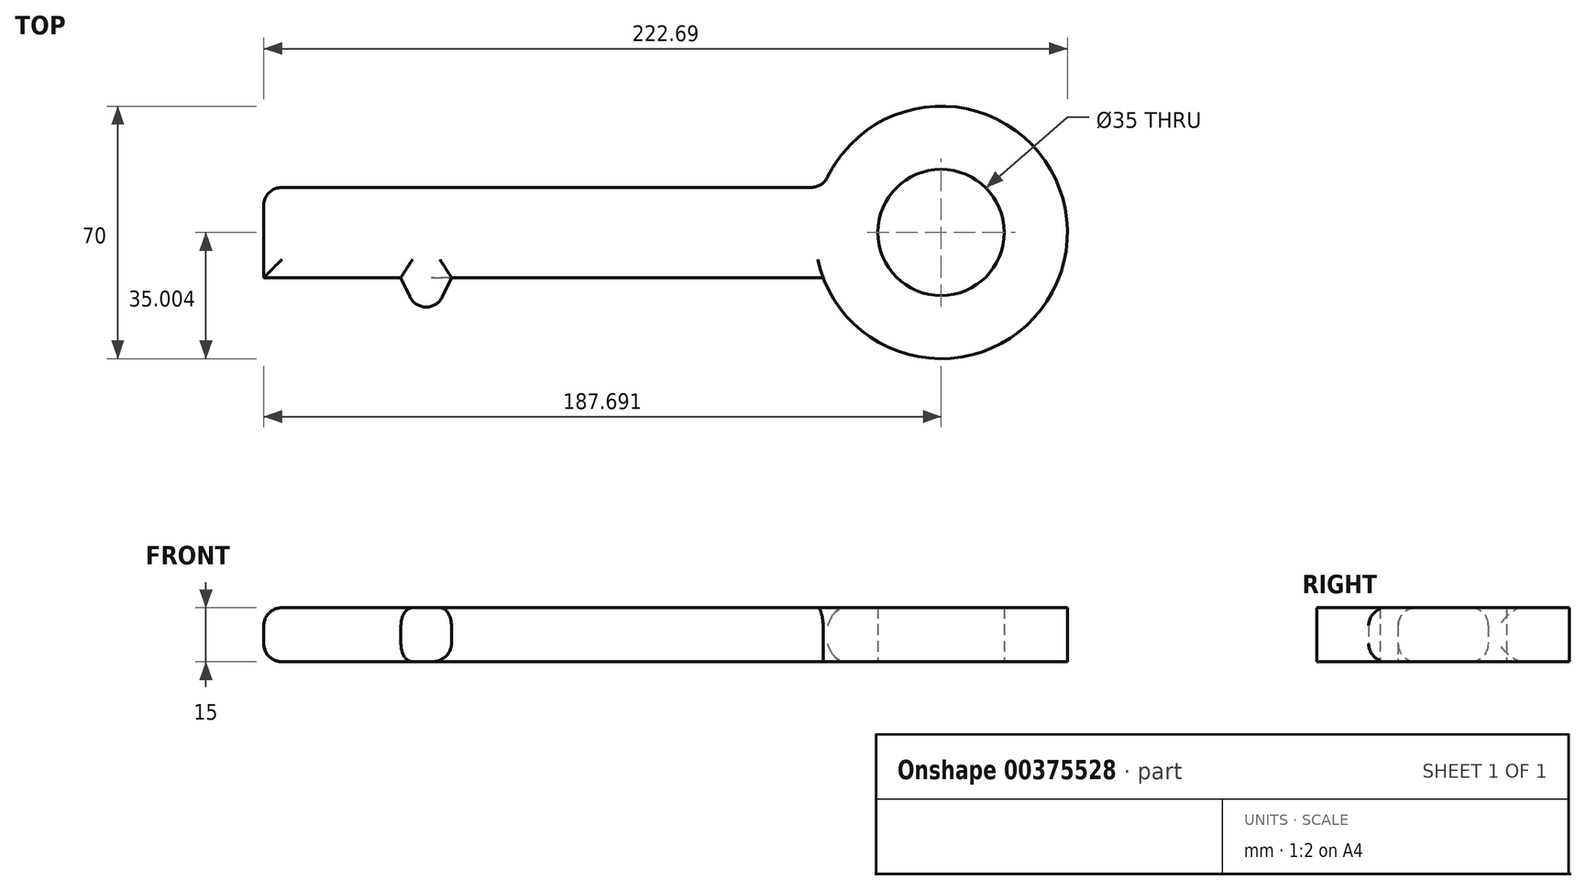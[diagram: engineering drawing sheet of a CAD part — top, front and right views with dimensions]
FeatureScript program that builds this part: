
annotation { "Feature Type Name" : "Feature", "Feature Type Description" : "" }
export const myFeature = defineFeature(function(context is Context, id is Id, definition is map)
    precondition{}
    {
        {
            var Q0;
            Q0=qCreatedBy(makeId("Top.planeOp"),FACE);
            var sketch = newSketch(context, id + "F0", { "sketchPlane" : qUnion([Q0])});
            skLineSegment(sketch, "E0.bottom", {"start": v(-78.27, 57.92) * mm, "end": v(76.73, 57.92) * mm});
            skLineSegment(sketch, "E0.top", {"start": v(-78.27, 32.92) * mm, "end": v(76.73, 32.92) * mm});
            skLineSegment(sketch, "E0.left", {"start": v(-78.27, 57.92) * mm, "end": v(-78.27, 32.92) * mm});
            skLineSegment(sketch, "E0.right", {"start": v(76.73, 57.92) * mm, "end": v(76.73, 32.92) * mm});
            skLineSegment(sketch, "E1.bottom", {"start": v(-78.27, 32.92) * mm, "end": v(-68.27, 32.92) * mm});
            skLineSegment(sketch, "E1.top", {"start": v(-78.27, 2.92) * mm, "end": v(-68.27, 2.92) * mm});
            skLineSegment(sketch, "E1.left", {"start": v(-78.27, 32.92) * mm, "end": v(-78.27, 2.92) * mm});
            skLineSegment(sketch, "E1.right", {"start": v(-68.27, 32.92) * mm, "end": v(-68.27, 2.92) * mm});
            skLineSegment(sketch, "E2.bottom", {"start": v(-58.27, 32.92) * mm, "end": v(-50.27, 32.92) * mm});
            skLineSegment(sketch, "E2.top", {"start": v(-58.27, 17.92) * mm, "end": v(-50.27, 17.92) * mm});
            skLineSegment(sketch, "E2.left", {"start": v(-58.27, 32.92) * mm, "end": v(-58.27, 17.92) * mm});
            skLineSegment(sketch, "E2.right", {"start": v(-50.27, 32.92) * mm, "end": v(-50.27, 17.92) * mm});
            skLineSegment(sketch, "E3", {"start": v(-33.27, 17.92) * mm, "end": v(-40.27, 32.92) * mm});
            skLineSegment(sketch, "E4", {"start": v(-40.27, 32.92) * mm, "end": v(-26.27, 32.92) * mm});
            skLineSegment(sketch, "E5", {"start": v(-26.27, 32.92) * mm, "end": v(-33.27, 17.92) * mm});
            skArc(sketch, "E6", {"start": v(76.73, 32.92) * mm, "mid": v(144.42, 45.42) * mm, "end": v(76.73, 57.92) * mm});
            skCircle(sketch, "E7", {"center": v(109.42, 45.42) * mm, "radius": 17.5 * mm});
            skSolve(sketch);
        }
        {
            var Q0;
            Q0=makeQuery(id+"F0.imprint","IMPRINT",FACE,{"disambiguationData":[TD([[makeQuery(id+"F0.imprint","IMPRINT",EDGE,{"derivedFrom":sQuery(id+"F0.wireOp",EDGE,"E0.bottom")}),-1.0]])]});
            var Q1;
            Q1=makeQuery(id+"F0.imprint","IMPRINT",FACE,{"disambiguationData":[TD([[makeQuery(id+"F0.imprint","IMPRINT",EDGE,{"derivedFrom":sQuery(id+"F0.wireOp",EDGE,"E3")}),-1.0]])]});
            var Q2;
            Q2=makeQuery(id+"F0.imprint","IMPRINT",FACE,{"disambiguationData":[TD([[makeQuery(id+"F0.imprint","IMPRINT",EDGE,{"derivedFrom":sQuery(id+"F0.wireOp",EDGE,"E2.bottom")}),-1.0]])]});
            var Q3;
            Q3=makeQuery(id+"F0.imprint","IMPRINT",FACE,{"disambiguationData":[TD([[makeQuery(id+"F0.imprint","IMPRINT",EDGE,{"derivedFrom":sQuery(id+"F0.wireOp",EDGE,"E1.bottom")}),-1.0]])]});
            var Q4;
            Q4=makeQuery(id+"F0.imprint","IMPRINT",FACE,{"disambiguationData":[TD([[makeQuery(id+"F0.imprint","IMPRINT",EDGE,{"derivedFrom":sQuery(id+"F0.wireOp",EDGE,"E0.right")}),1.0]])]});
            extrude(context, id + "F1", {"entities" : qUnion([Q0, Q1, Q2, Q3, Q4]), "depth" : 15 * mm});
        }
        {
            var Q0;
            Q0=makeQuery(id+"F1.opExtrude","CAP_EDGE",EDGE,{"disambiguationData":[OSD([sQuery(id+"F0.wireOp",EDGE,"E0.left"),sQuery(id+"F0.wireOp",EDGE,"E1.left")])],"isStart":false});
            var Q1;
            Q1=makeQuery(id+"F1.opExtrude","CAP_EDGE",EDGE,{"disambiguationData":[OSD([sQuery(id+"F0.wireOp",EDGE,"E1.right")])],"isStart":false});
            var Q2;
            {var subQ0=sQuery(id+"F0.wireOp",EDGE,"E0.top");Q2=makeQuery(id+"F1.opExtrude","CAP_EDGE",EDGE,{"disambiguationData":[OSD([subQ0]),TDD([makeQuery(id+"F0.imprint","IMPRINT",EDGE,{"disambiguationData":[TD([[makeQuery(id+"F0.imprint","INTERSECT",VERTEX,{"derivedFrom":[subQ0,sQuery(id+"F0.wireOp",EDGE,"E1.bottom"),sQuery(id+"F0.wireOp",EDGE,"E1.right")]}),-1.0]])],"derivedFrom":subQ0})])],"isStart":false});}
            var Q3;
            Q3=makeQuery(id+"F1.opExtrude","CAP_EDGE",EDGE,{"disambiguationData":[OSD([sQuery(id+"F0.wireOp",EDGE,"E2.left")])],"isStart":false});
            var Q4;
            Q4=makeQuery(id+"F1.opExtrude","CAP_EDGE",EDGE,{"disambiguationData":[OSD([sQuery(id+"F0.wireOp",EDGE,"E2.top")])],"isStart":false});
            var Q5;
            Q5=makeQuery(id+"F1.opExtrude","CAP_EDGE",EDGE,{"disambiguationData":[OSD([sQuery(id+"F0.wireOp",EDGE,"E2.right")])],"isStart":false});
            var Q6;
            Q6=makeQuery(id+"F1.opExtrude","CAP_EDGE",EDGE,{"disambiguationData":[OSD([sQuery(id+"F0.wireOp",EDGE,"E1.top")])],"isStart":false});
            var Q7;
            {var subQ0=sQuery(id+"F0.wireOp",EDGE,"E0.top");Q7=makeQuery(id+"F1.opExtrude","CAP_EDGE",EDGE,{"disambiguationData":[OSD([subQ0]),TDD([makeQuery(id+"F0.imprint","IMPRINT",EDGE,{"disambiguationData":[TD([[makeQuery(id+"F0.imprint","INTERSECT",VERTEX,{"derivedFrom":[subQ0,sQuery(id+"F0.wireOp",EDGE,"E2.bottom"),sQuery(id+"F0.wireOp",EDGE,"E2.right")]}),-1.0]])],"derivedFrom":subQ0})])],"isStart":false});}
            var Q8;
            Q8=makeQuery(id+"F1.opExtrude","CAP_EDGE",EDGE,{"disambiguationData":[OSD([sQuery(id+"F0.wireOp",EDGE,"E3")])],"isStart":false});
            var Q9;
            Q9=makeQuery(id+"F1.opExtrude","CAP_EDGE",EDGE,{"disambiguationData":[OSD([sQuery(id+"F0.wireOp",EDGE,"E5")])],"isStart":false});
            var Q10;
            {var subQ0=sQuery(id+"F0.wireOp",EDGE,"E0.top");Q10=makeQuery(id+"F1.opExtrude","CAP_EDGE",EDGE,{"disambiguationData":[OSD([subQ0]),TDD([makeQuery(id+"F0.imprint","IMPRINT",EDGE,{"disambiguationData":[TD([[makeQuery(id+"F0.imprint","INTERSECT",VERTEX,{"derivedFrom":[subQ0,sQuery(id+"F0.wireOp",EDGE,"E0.right"),sQuery(id+"F0.wireOp",EDGE,"E6")]}),1.0]])],"derivedFrom":subQ0})])],"isStart":false});}
            var Q11;
            Q11=makeQuery(id+"F1.opExtrude","CAP_EDGE",EDGE,{"disambiguationData":[OSD([sQuery(id+"F0.wireOp",EDGE,"E0.bottom")])],"isStart":false});
            var Q12;
            Q12=makeQuery(id+"F1.opExtrude","CAP_EDGE",EDGE,{"disambiguationData":[OSD([sQuery(id+"F0.wireOp",EDGE,"E5")])],"isStart":true});
            var Q13;
            Q13=makeQuery(id+"F1.opExtrude","SWEPT_EDGE",EDGE,{"disambiguationData":[OSD([sQuery(id+"F0.wireOp",EDGE,"E3"),sQuery(id+"F0.wireOp",EDGE,"E5")])]});
            var Q14;
            Q14=makeQuery(id+"F1.opExtrude","SWEPT_EDGE",EDGE,{"disambiguationData":[OSD([sQuery(id+"F0.wireOp",EDGE,"E1.top"),sQuery(id+"F0.wireOp",EDGE,"E1.right")])]});
            var Q15;
            Q15=makeQuery(id+"F1.opExtrude","CAP_EDGE",EDGE,{"disambiguationData":[OSD([sQuery(id+"F0.wireOp",EDGE,"E1.right")])],"isStart":true});
            var Q16;
            Q16=makeQuery(id+"F1.opExtrude","CAP_EDGE",EDGE,{"disambiguationData":[OSD([sQuery(id+"F0.wireOp",EDGE,"E0.left"),sQuery(id+"F0.wireOp",EDGE,"E1.left")])],"isStart":true});
            var Q17;
            Q17=makeQuery(id+"F1.opExtrude","SWEPT_EDGE",EDGE,{"disambiguationData":[OSD([sQuery(id+"F0.wireOp",EDGE,"E0.bottom"),sQuery(id+"F0.wireOp",EDGE,"E0.left")])]});
            var Q18;
            Q18=makeQuery(id+"F1.opExtrude","CAP_EDGE",EDGE,{"disambiguationData":[OSD([sQuery(id+"F0.wireOp",EDGE,"E3")])],"isStart":true});
            var Q19;
            {var subQ0=sQuery(id+"F0.wireOp",EDGE,"E0.top");Q19=makeQuery(id+"F1.opExtrude","CAP_EDGE",EDGE,{"disambiguationData":[OSD([subQ0]),TDD([makeQuery(id+"F0.imprint","IMPRINT",EDGE,{"disambiguationData":[TD([[makeQuery(id+"F0.imprint","INTERSECT",VERTEX,{"derivedFrom":[subQ0,sQuery(id+"F0.wireOp",EDGE,"E2.bottom"),sQuery(id+"F0.wireOp",EDGE,"E2.right")]}),-1.0]])],"derivedFrom":subQ0})])],"isStart":true});}
            var Q20;
            Q20=makeQuery(id+"F1.opExtrude","CAP_EDGE",EDGE,{"disambiguationData":[OSD([sQuery(id+"F0.wireOp",EDGE,"E2.left")])],"isStart":true});
            var Q21;
            {var subQ0=sQuery(id+"F0.wireOp",EDGE,"E0.top");Q21=makeQuery(id+"F1.opExtrude","CAP_EDGE",EDGE,{"disambiguationData":[OSD([subQ0]),TDD([makeQuery(id+"F0.imprint","IMPRINT",EDGE,{"disambiguationData":[TD([[makeQuery(id+"F0.imprint","INTERSECT",VERTEX,{"derivedFrom":[subQ0,sQuery(id+"F0.wireOp",EDGE,"E1.bottom"),sQuery(id+"F0.wireOp",EDGE,"E1.right")]}),-1.0]])],"derivedFrom":subQ0})])],"isStart":true});}
            var Q22;
            Q22=makeQuery(id+"F1.opExtrude","SWEPT_FACE",FACE,{"disambiguationData":[OSD([sQuery(id+"F0.wireOp",EDGE,"E0.bottom")])]});
            var Q23;
            Q23=makeQuery(id+"F1.opExtrude","CAP_EDGE",EDGE,{"disambiguationData":[OSD([sQuery(id+"F0.wireOp",EDGE,"E2.top")])],"isStart":true});
            var Q24;
            Q24=makeQuery(id+"F1.opExtrude","CAP_EDGE",EDGE,{"disambiguationData":[OSD([sQuery(id+"F0.wireOp",EDGE,"E1.top")])],"isStart":true});
            var Q25;
            Q25=makeQuery(id+"F1.opExtrude","CAP_EDGE",EDGE,{"disambiguationData":[OSD([sQuery(id+"F0.wireOp",EDGE,"E2.right")])],"isStart":true});
            fillet(context, id + "F2", {"entities" : qUnion([Q0, Q1, Q2, Q3, Q4, Q5, Q6, Q7, Q8, Q9, Q10, Q11, Q12, Q13, Q14, Q15, Q16, Q17, Q18, Q19, Q20, Q21, Q22, Q23, Q24, Q25]), "radius" : 5 * mm, "tangentPropagation" : true, "allowEdgeOverflow" : false});
        }
    });
